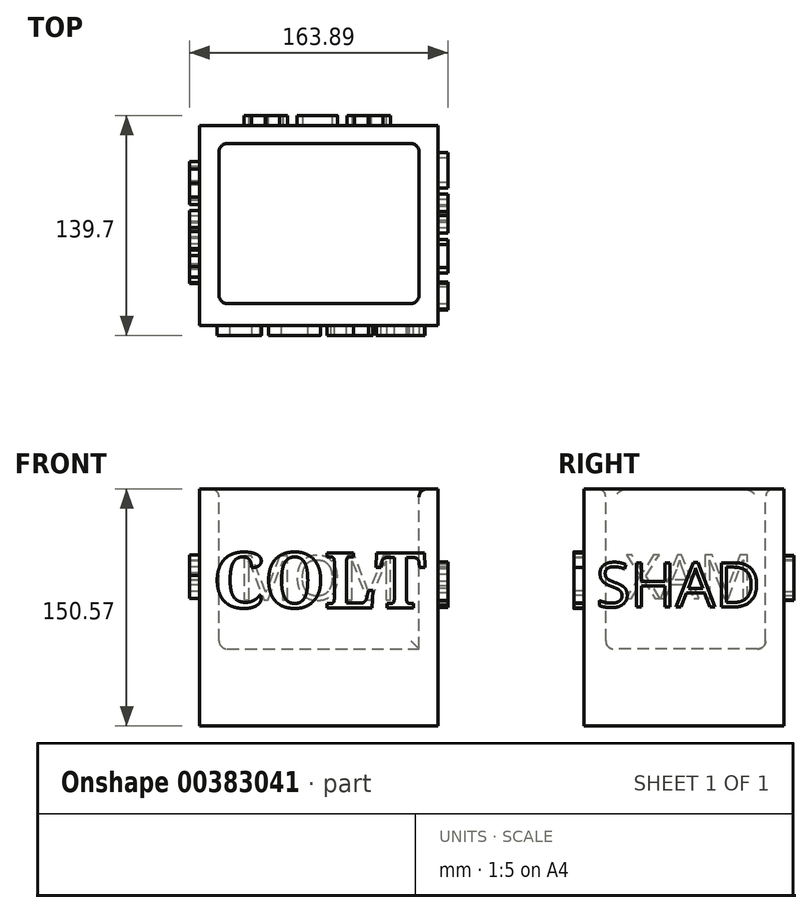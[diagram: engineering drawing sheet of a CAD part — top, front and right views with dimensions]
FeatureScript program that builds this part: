
annotation { "Feature Type Name" : "Feature", "Feature Type Description" : "" }
export const myFeature = defineFeature(function(context is Context, id is Id, definition is map)
    precondition{}
    {
        {
            var Q0;
            Q0=qCreatedBy(makeId("Front.planeOp"),FACE);
            var sketch = newSketch(context, id + "F0", { "sketchPlane" : qUnion([Q0])});
            skLineSegment(sketch, "E0.bottom", {"start": v(75.9, -75.13) * mm, "end": v(-75.29, -75.13) * mm});
            skLineSegment(sketch, "E0.top", {"start": v(75.9, 75.44) * mm, "end": v(-75.29, 75.44) * mm});
            skLineSegment(sketch, "E0.left", {"start": v(75.9, -75.13) * mm, "end": v(75.9, 75.44) * mm});
            skLineSegment(sketch, "E0.right", {"start": v(-75.29, -75.13) * mm, "end": v(-75.29, 75.44) * mm});
            skSolve(sketch);
        }
        {
            var Q0;
            Q0 = qSketchRegion(id + "F0", true);
            extrude(context, id + "F1", {"entities" : qUnion([Q0]), "depth" : 127 * mm});
        }
        {
            var Q0;
            Q0=makeQuery(id+"F1.opExtrude","CAP_FACE",FACE,{"disambiguationData":[OSD([sQuery(id+"F0.wireOp",EDGE,"E0.bottom"),sQuery(id+"F0.wireOp",EDGE,"E0.top"),sQuery(id+"F0.wireOp",EDGE,"E0.left"),sQuery(id+"F0.wireOp",EDGE,"E0.right")])],"isStart":false});
            var sketch = newSketch(context, id + "F2", { "sketchPlane" : qUnion([Q0])});
            skText(sketch, "E1", { "text": "COLT", "fontName": "NotoSerif-Bold.ttf"});
            const initialGuessF2  = {"E1": [-0.0669, 0, 1, 0, 0.0352]};
            skSetInitialGuess(sketch, initialGuessF2);
            skSolve(sketch);
        }
        {
            var Q0;
            Q0=makeQuery(id+"F2.imprint","IMPRINT",FACE,{"disambiguationData":[TD([[makeQuery(id+"F2.imprint","IMPRINT",EDGE,{"derivedFrom":sQuery(id+"F2.wireOp",EDGE,"E1.sketch_text.stroke-38")}),-1.0]])]});
            var Q1;
            Q1=makeQuery(id+"F2.imprint","IMPRINT",FACE,{"disambiguationData":[TD([[makeQuery(id+"F2.imprint","IMPRINT",EDGE,{"derivedFrom":sQuery(id+"F2.wireOp",EDGE,"E1.sketch_text.stroke-70")}),-1.0]])]});
            var Q2;
            Q2=makeQuery(id+"F2.imprint","IMPRINT",FACE,{"disambiguationData":[TD([[makeQuery(id+"F2.imprint","IMPRINT",EDGE,{"derivedFrom":sQuery(id+"F2.wireOp",EDGE,"E1.sketch_text.stroke-98")}),-1.0]])]});
            var Q3;
            Q3=makeQuery(id+"F2.imprint","IMPRINT",FACE,{"disambiguationData":[TD([[makeQuery(id+"F2.imprint","IMPRINT",EDGE,{"derivedFrom":sQuery(id+"F2.wireOp",EDGE,"E1.sketch_text.stroke-0")}),-1.0]])]});
            extrude(context, id + "F3", {"entities" : qUnion([Q0, Q1, Q2, Q3]), "operationType" : NewBodyOperationType.ADD, "depth" : 6.35 * mm});
        }
        {
            var Q0;
            Q0=makeQuery(id+"F1.opExtrude","SWEPT_FACE",FACE,{"disambiguationData":[OSD([sQuery(id+"F0.wireOp",EDGE,"E0.top")])]});
            var sketch = newSketch(context, id + "F4", { "sketchPlane" : qUnion([Q0])});
            skLineSegment(sketch, "E2.bottom", {"start": v(-63.06, -11.43) * mm, "end": v(63.94, -11.43) * mm});
            skLineSegment(sketch, "E2.top", {"start": v(-63.06, -113.03) * mm, "end": v(63.94, -113.03) * mm});
            skLineSegment(sketch, "E2.left", {"start": v(-63.06, -11.43) * mm, "end": v(-63.06, -113.03) * mm});
            skLineSegment(sketch, "E2.right", {"start": v(63.94, -11.43) * mm, "end": v(63.94, -113.03) * mm});
            skSolve(sketch);
        }
        {
            var Q0;
            Q0=makeQuery(id+"F4.imprint","IMPRINT",FACE,{"disambiguationData":[TD([[makeQuery(id+"F4.imprint","IMPRINT",EDGE,{"derivedFrom":sQuery(id+"F4.wireOp",EDGE,"E2.bottom")}),-1.0]])]});
            extrude(context, id + "F5", {"entities" : qUnion([Q0]), "operationType" : NewBodyOperationType.REMOVE, "oppositeDirection" : true, "depth" : 101.6 * mm});
        }
        {
            var Q0;
            Q0=makeQuery(id+"F1.opExtrude","SWEPT_FACE",FACE,{"disambiguationData":[OSD([sQuery(id+"F0.wireOp",EDGE,"E0.left")])]});
            var sketch = newSketch(context, id + "F6", { "sketchPlane" : qUnion([Q0])});
            skText(sketch, "E3", { "text": "SHAD", "fontName": "OpenSans-Regular.ttf"});
            const initialGuessF6  = {"E3": [-0.1191, 0.00046, 1, 0, 0.02835]};
            skSetInitialGuess(sketch, initialGuessF6);
            skSolve(sketch);
        }
        {
            var Q0;
            Q0 = qSketchRegion(id + "F6", true);
            extrude(context, id + "F7", {"entities" : qUnion([Q0]), "operationType" : NewBodyOperationType.ADD, "depth" : 6.35 * mm});
        }
        {
            var Q0;
            Q0=makeQuery(id+"F1.opExtrude","SWEPT_FACE",FACE,{"disambiguationData":[OSD([sQuery(id+"F0.wireOp",EDGE,"E0.right")])]});
            var sketch = newSketch(context, id + "F8", { "sketchPlane" : qUnion([Q0])});
            skText(sketch, "E4", { "text": "MAX", "fontName": "OpenSans-Regular.ttf"});
            const initialGuessF8  = {"E4": [0.01913, 0.00594, 1, 0, 0.02774]};
            skSetInitialGuess(sketch, initialGuessF8);
            skSolve(sketch);
        }
        {
            var Q0;
            Q0 = qSketchRegion(id + "F8", true);
            extrude(context, id + "F9", {"entities" : qUnion([Q0]), "operationType" : NewBodyOperationType.ADD, "depth" : 6.35 * mm});
        }
        {
            var Q0;
            Q0=makeQuery(id+"F1.opExtrude","CAP_FACE",FACE,{"disambiguationData":[OSD([sQuery(id+"F0.wireOp",EDGE,"E0.bottom"),sQuery(id+"F0.wireOp",EDGE,"E0.top"),sQuery(id+"F0.wireOp",EDGE,"E0.left"),sQuery(id+"F0.wireOp",EDGE,"E0.right")])],"isStart":true});
            var sketch = newSketch(context, id + "F10", { "sketchPlane" : qUnion([Q0])});
            skText(sketch, "E5", { "text": "MOM\n", "fontName": "OpenSans-Regular.ttf"});
            const initialGuessF10  = {"E5": [-0.04968, 0.00503, 1, 0, 0.02804]};
            skSetInitialGuess(sketch, initialGuessF10);
            skSolve(sketch);
        }
        {
            var Q0;
            Q0 = qSketchRegion(id + "F10", true);
            extrude(context, id + "F11", {"entities" : qUnion([Q0]), "operationType" : NewBodyOperationType.ADD, "depth" : 6.35 * mm});
        }
        {
            var Q0;
            Q0=makeQuery(id+"F5.boolean.opBoolean","COPY",EDGE,{"derivedFrom":makeQuery(id+"F5.opExtrude","CAP_EDGE",EDGE,{"disambiguationData":[OSD([sQuery(id+"F4.wireOp",EDGE,"E2.left")])],"isStart":true})});
            var Q1;
            Q1=makeQuery(id+"F5.boolean.opBoolean","COPY",EDGE,{"derivedFrom":makeQuery(id+"F5.opExtrude","CAP_EDGE",EDGE,{"disambiguationData":[OSD([sQuery(id+"F4.wireOp",EDGE,"E2.bottom")])],"isStart":true})});
            var Q2;
            Q2=makeQuery(id+"F5.boolean.opBoolean","COPY",EDGE,{"derivedFrom":makeQuery(id+"F5.opExtrude","CAP_EDGE",EDGE,{"disambiguationData":[OSD([sQuery(id+"F4.wireOp",EDGE,"E2.right")])],"isStart":true})});
            var Q3;
            Q3=makeQuery(id+"F5.boolean.opBoolean","COPY",EDGE,{"derivedFrom":makeQuery(id+"F5.opExtrude","CAP_EDGE",EDGE,{"disambiguationData":[OSD([sQuery(id+"F4.wireOp",EDGE,"E2.top")])],"isStart":true})});
            var Q4;
            Q4=makeQuery(id+"F5.boolean.opBoolean","COPY",FACE,{"derivedFrom":makeQuery(id+"F5.opExtrude","SWEPT_FACE",FACE,{"disambiguationData":[OSD([sQuery(id+"F4.wireOp",EDGE,"E2.bottom")])]})});
            var Q5;
            Q5=makeQuery(id+"F5.boolean.opBoolean","COPY",FACE,{"derivedFrom":makeQuery(id+"F5.opExtrude","SWEPT_FACE",FACE,{"disambiguationData":[OSD([sQuery(id+"F4.wireOp",EDGE,"E2.left")])]})});
            var Q6;
            Q6=makeQuery(id+"F5.boolean.opBoolean","COPY",FACE,{"derivedFrom":makeQuery(id+"F5.opExtrude","SWEPT_FACE",FACE,{"disambiguationData":[OSD([sQuery(id+"F4.wireOp",EDGE,"E2.top")])]})});
            fillet(context, id + "F12", {"entities" : qUnion([Q0, Q1, Q2, Q3, Q4, Q5, Q6]), "radius" : 5.08 * mm, "tangentPropagation" : true, "allowEdgeOverflow" : false});
        }
    });
